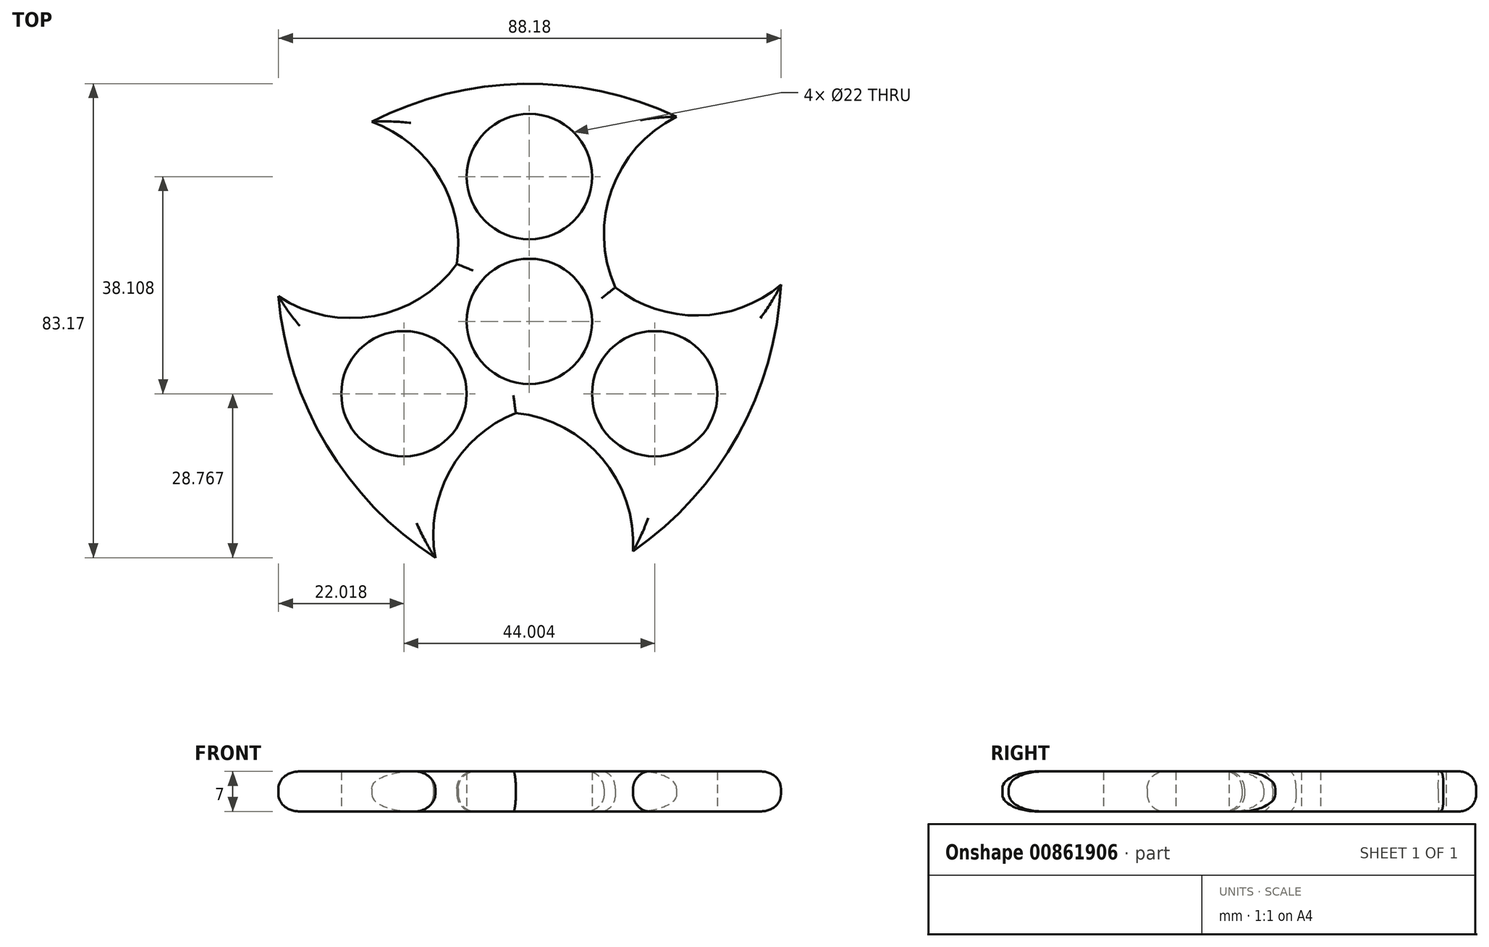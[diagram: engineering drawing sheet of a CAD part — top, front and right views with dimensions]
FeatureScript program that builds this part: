
annotation { "Feature Type Name" : "Feature", "Feature Type Description" : "" }
export const myFeature = defineFeature(function(context is Context, id is Id, definition is map)
    precondition{}
    {
        {
            var Q0;
            Q0=qCreatedBy(makeId("Top.planeOp"),FACE);
            var sketch = newSketch(context, id + "F0", { "sketchPlane" : qUnion([Q0])});
            skCircle(sketch, "E0", {"center": v(0, 0) * mm, "radius": 11 * mm});
            skCircle(sketch, "E1", {"center": v(0, 25.4) * mm, "radius": 11 * mm});
            skArc(sketch, "E2", {"start": v(25.83, 35.92) * mm, "mid": v(-1.02, 41.69) * mm, "end": v(-27.66, 35.02) * mm});
            skArc(sketch, "E3", {"start": v(-16.77, 0) * mm, "mid": v(-13.51, 20.22) * mm, "end": v(-27.66, 35.02) * mm});
            skArc(sketch, "E4", {"start": v(25.83, 35.92) * mm, "mid": v(13.5, 19.66) * mm, "end": v(18.95, 0) * mm});
            skArc(sketch, "E5.1.0", {"start": v(-44.02, 4.41) * mm, "mid": v(-35.6, -21.73) * mm, "end": v(-16.5, -41.47) * mm});
            skCircle(sketch, "E5.1.1", {"center": v(-22, -12.7) * mm, "radius": 11 * mm});
            skArc(sketch, "E5.1.2", {"start": v(-44.02, 4.41) * mm, "mid": v(-23.78, 1.86) * mm, "end": v(-9.48, 16.41) * mm});
            skArc(sketch, "E5.1.3", {"start": v(8.39, -14.52) * mm, "mid": v(-10.75, -21.81) * mm, "end": v(-16.5, -41.47) * mm});
            skArc(sketch, "E5.2.0", {"start": v(18.2, -40.33) * mm, "mid": v(36.61, -19.96) * mm, "end": v(44.16, 6.45) * mm});
            skCircle(sketch, "E5.2.1", {"center": v(22, -12.7) * mm, "radius": 11 * mm});
            skArc(sketch, "E5.2.2", {"start": v(18.2, -40.33) * mm, "mid": v(10.28, -21.53) * mm, "end": v(-9.48, -16.41) * mm});
            skArc(sketch, "E5.2.3", {"start": v(8.39, 14.52) * mm, "mid": v(24.26, 1.6) * mm, "end": v(44.16, 6.45) * mm});
            skSolve(sketch);
        }
        {
            var Q0;
            Q0 = qSketchRegion(id + "F0", true);
            extrude(context, id + "F1", {"entities" : qUnion([Q0]), "depth" : 7 * mm, "offsetDistance" : 25 * mm});
        }
        {
            var Q0;
            Q0=makeQuery(id+"F1.opExtrude","CAP_EDGE",EDGE,{"disambiguationData":[OSD([sQuery(id+"F0.wireOp",EDGE,"E4")])],"isStart":false});
            var Q1;
            Q1=makeQuery(id+"F1.opExtrude","CAP_EDGE",EDGE,{"disambiguationData":[OSD([sQuery(id+"F0.wireOp",EDGE,"E5.2.3")])],"isStart":false});
            var Q2;
            Q2=makeQuery(id+"F1.opExtrude","CAP_EDGE",EDGE,{"disambiguationData":[OSD([sQuery(id+"F0.wireOp",EDGE,"E5.2.0")])],"isStart":false});
            var Q3;
            Q3=makeQuery(id+"F1.opExtrude","CAP_EDGE",EDGE,{"disambiguationData":[OSD([sQuery(id+"F0.wireOp",EDGE,"E5.2.2")])],"isStart":false});
            var Q4;
            Q4=makeQuery(id+"F1.opExtrude","CAP_EDGE",EDGE,{"disambiguationData":[OSD([sQuery(id+"F0.wireOp",EDGE,"E5.1.3")])],"isStart":false});
            var Q5;
            Q5=makeQuery(id+"F1.opExtrude","CAP_EDGE",EDGE,{"disambiguationData":[OSD([sQuery(id+"F0.wireOp",EDGE,"E5.1.0")])],"isStart":false});
            var Q6;
            Q6=makeQuery(id+"F1.opExtrude","CAP_EDGE",EDGE,{"disambiguationData":[OSD([sQuery(id+"F0.wireOp",EDGE,"E5.1.2")])],"isStart":false});
            var Q7;
            Q7=makeQuery(id+"F1.opExtrude","CAP_EDGE",EDGE,{"disambiguationData":[OSD([sQuery(id+"F0.wireOp",EDGE,"E3")])],"isStart":false});
            var Q8;
            Q8=makeQuery(id+"F1.opExtrude","CAP_EDGE",EDGE,{"disambiguationData":[OSD([sQuery(id+"F0.wireOp",EDGE,"E2")])],"isStart":false});
            fillet(context, id + "F2", {"entities" : qUnion([Q0, Q1, Q2, Q3, Q4, Q5, Q6, Q7, Q8]), "radius" : 3 * mm, "tangentPropagation" : true, "allowEdgeOverflow" : false});
        }
        {
            var Q0;
            Q0=makeQuery(id+"F1.opExtrude","CAP_EDGE",EDGE,{"disambiguationData":[OSD([sQuery(id+"F0.wireOp",EDGE,"E2")])],"isStart":true});
            var Q1;
            Q1=makeQuery(id+"F1.opExtrude","CAP_EDGE",EDGE,{"disambiguationData":[OSD([sQuery(id+"F0.wireOp",EDGE,"E4")])],"isStart":true});
            var Q2;
            Q2=makeQuery(id+"F1.opExtrude","CAP_EDGE",EDGE,{"disambiguationData":[OSD([sQuery(id+"F0.wireOp",EDGE,"E3")])],"isStart":true});
            var Q3;
            Q3=makeQuery(id+"F1.opExtrude","CAP_EDGE",EDGE,{"disambiguationData":[OSD([sQuery(id+"F0.wireOp",EDGE,"E5.2.3")])],"isStart":true});
            var Q4;
            Q4=makeQuery(id+"F1.opExtrude","CAP_EDGE",EDGE,{"disambiguationData":[OSD([sQuery(id+"F0.wireOp",EDGE,"E5.2.0")])],"isStart":true});
            var Q5;
            Q5=makeQuery(id+"F1.opExtrude","CAP_EDGE",EDGE,{"disambiguationData":[OSD([sQuery(id+"F0.wireOp",EDGE,"E5.2.2")])],"isStart":true});
            var Q6;
            Q6=makeQuery(id+"F1.opExtrude","CAP_EDGE",EDGE,{"disambiguationData":[OSD([sQuery(id+"F0.wireOp",EDGE,"E5.1.3")])],"isStart":true});
            var Q7;
            Q7=makeQuery(id+"F1.opExtrude","CAP_EDGE",EDGE,{"disambiguationData":[OSD([sQuery(id+"F0.wireOp",EDGE,"E5.1.0")])],"isStart":true});
            var Q8;
            Q8=makeQuery(id+"F1.opExtrude","CAP_EDGE",EDGE,{"disambiguationData":[OSD([sQuery(id+"F0.wireOp",EDGE,"E5.1.2")])],"isStart":true});
            fillet(context, id + "F3", {"entities" : qUnion([Q0, Q1, Q2, Q3, Q4, Q5, Q6, Q7, Q8]), "radius" : 3 * mm, "tangentPropagation" : true, "allowEdgeOverflow" : false});
        }
    });
